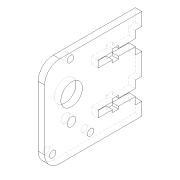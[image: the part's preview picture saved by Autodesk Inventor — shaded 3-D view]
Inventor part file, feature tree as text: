
AUTODESK INVENTOR PART (.ipt)
format: ipt  version: 2016 (Build 200138000, 138)  size: 180,224 bytes
history: native  units: mm
features: extrude x3, sketch x3, fillet x1
ambient origin geometry x8: Origin, YZ Plane, XZ Plane, XY Plane, X Axis, Y Axis, Z Axis, Center Point
bodies: Solid1 (feature_tree)
feature tree (7):
  extrude  "Extrusion1"  Depth=42.0mm
  extrude  "Extrusion4"  Depth=3.0mm
  extrude  "Extrusion5"  Depth=3.0mm
  fillet  "Fillet2"  Radius=10.0mm
  sketch  "Sketch1"  dims[d0=45.0mm d1=42.0mm]
  sketch  "Sketch4"  dims[d2=3.0mm d3=0.0mm d21=3.0mm]
  sketch  "Sketch5"  dims[d23=3.0mm d26=3.0mm d29=10.0mm d32=12.5mm d35=4.0mm d36=0.0mm d38=10.0mm d42=6.0mm d44=4.0mm d45=0.0mm d46=7.0mm d47=10.0mm d48=10.0mm d55=2.75mm d59=3.0mm d60=7.8mm d61=6.65mm d62=5.6mm d63=3.2mm d64=3.4mm d65=3.4mm d66=7.8mm d67=1.2mm d68=1.2mm d69=2.75mm d70=3.2mm d71=1.2mm d72=1.2mm d73=6.65mm d74=7.8mm d75=20.2mm d76=4.0mm d77=4.0mm d78=12.5mm d79=7.9mm]
